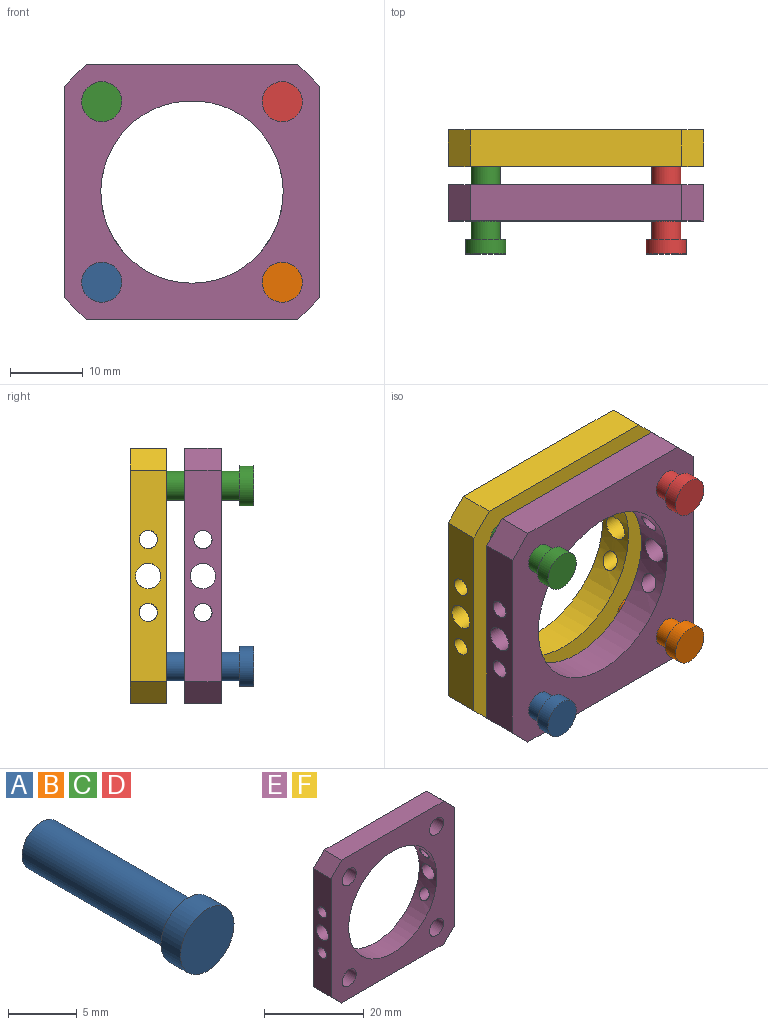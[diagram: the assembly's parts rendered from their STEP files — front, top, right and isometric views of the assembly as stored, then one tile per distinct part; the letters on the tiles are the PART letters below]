
ASSEMBLY  parts=6 mates=5
PART A: 5 faces, bbox 5.5x17x5.5 mm
  f0: cylinder r=2mm len=15mm, axis (0,1,0), area 188.5mm2, adj f1,f4
  f1: plane 4x4mm, normal (0,1,0), area 12.6mm2, adj f0
  f2: cylinder r=2.75mm len=5.5mm, axis (0,1,0), area 34.6mm2, adj f3,f4
  f3: plane 5.5x5.5mm, normal (0,-1,0), area 23.8mm2, adj f2
  f4: plane 5.5x5.5mm, normal (0,1,0), area 11.2mm2, adj f0,f2
PART B: same geometry as A
PART C: same geometry as A
PART D: same geometry as A
PART E: 21 faces, bbox 35x5x35 mm
  f0: plane 5x3mm, normal (0.71,0,0.71), area 21.2mm2, adj f1,f11,f13,f14
  f1: plane 29x5mm, normal (0,0,1), area 145mm2, adj f0,f2,f13,f14
  f2: plane 5x3mm, normal (-0.71,0,0.71), area 21.2mm2, adj f1,f3,f13,f14
  f3: plane 29x5mm, normal (-1,0,0), area 125.6mm2, adj f2,f4,f13,f14,f18,f19,f20
  f4: plane 5x3mm, normal (-0.71,0,-0.71), area 21.2mm2, adj f3,f5,f13,f14
  f5: plane 29x5mm, normal (0,0,-1), area 145mm2, adj f4,f6,f13,f14
  f6: plane 5x3mm, normal (0.71,0,-0.71), area 21.2mm2, adj f5,f11,f13,f14
  f7: cylinder r=2mm len=5mm, axis (0,1,0), area 62.8mm2, adj f13,f14
  f8: cylinder r=2mm len=5mm, axis (0,1,0), area 62.8mm2, adj f13,f14
  f9: cylinder r=2mm len=5mm, axis (0,1,0), area 62.8mm2, adj f13,f14
  f10: cylinder r=12.5mm len=25mm, axis (0,1,0), area 351.9mm2, adj f13,f14,f15,f16,f17,f18,f19,f20
  f11: plane 29x5mm, normal (1,0,0), area 125.6mm2, adj f0,f6,f13,f14,f15,f16,f17
  f12: cylinder r=2mm len=5mm, axis (0,1,0), area 62.8mm2, adj f13,f14
  f13: plane 35x35mm, normal (0,-1,0), area 665.9mm2, adj f0,f1,f2,f3,f4,f5,f6,f7
  f14: plane 35x35mm, normal (0,1,0), area 665.9mm2, adj f0,f1,f2,f3,f4,f5,f6,f7
  f15: cylinder r=1.75mm len=5.12mm, axis (1,0,0), area 55.7mm2, adj f10,f11
  f16: cylinder r=1.25mm len=6.68mm, axis (1,0,0), area 47.8mm2, adj f10,f11
  f17: cylinder r=1.25mm len=6.67mm, axis (1,0,0), area 47.8mm2, adj f10,f11
  f18: cylinder r=1.75mm len=5.12mm, axis (1,0,0), area 55.7mm2, adj f3,f10
  f19: cylinder r=1.25mm len=6.68mm, axis (1,0,0), area 47.8mm2, adj f3,f10
  f20: cylinder r=1.25mm len=6.67mm, axis (1,0,0), area 47.8mm2, adj f3,f10
PART F: same geometry as E
PLACE A t=(-11.21,11.7,-12.55)mm
PLACE B t=(13.55,11.7,-12.55)mm
PLACE C t=(-11.21,11.7,12.21)mm
PLACE D t=(13.55,11.7,12.21)mm
PLACE E t=(1.17,4.2,-0.17)mm
PLACE F t=(1.17,11.7,-0.17)mm
MATE fastened C.f0 <-> F.f9  axis (0,1,0) through (-11.21,11.7,12.21)mm
MATE fastened A.f0 <-> F.f8  axis (0,1,0) through (-11.21,11.7,-12.55)mm
MATE fastened D.f0 <-> F.f12  axis (0,1,0) through (13.55,11.7,12.21)mm
MATE fastened B.f0 <-> F.f7  axis (0,1,0) through (13.55,11.7,-12.55)mm
MATE fastened E.f9 <-> C.f0  axis (0,1,0) through (-11.21,4.2,12.21)mm
